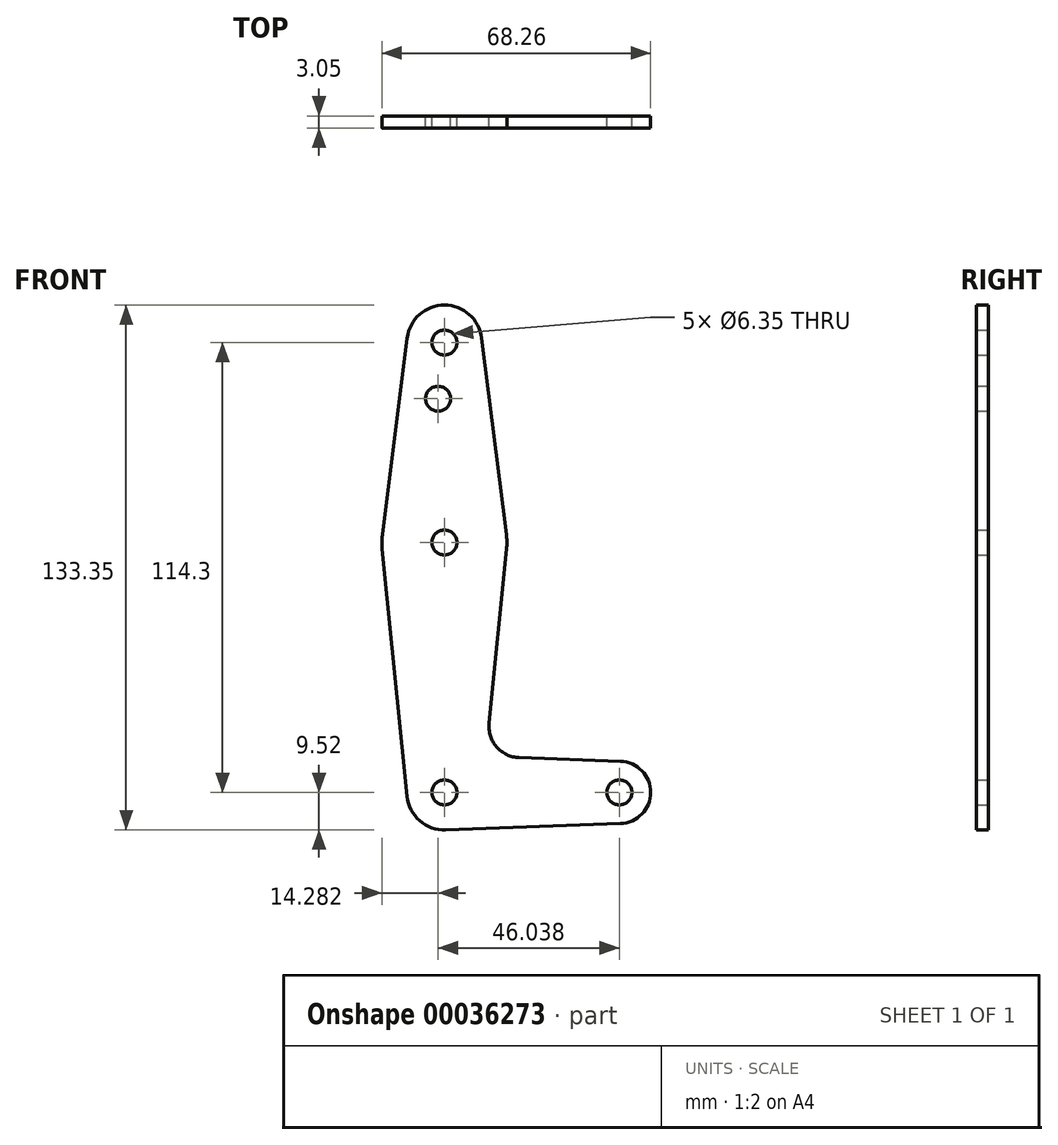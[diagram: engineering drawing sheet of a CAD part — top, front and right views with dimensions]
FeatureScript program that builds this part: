
annotation { "Feature Type Name" : "Feature", "Feature Type Description" : "" }
export const myFeature = defineFeature(function(context is Context, id is Id, definition is map)
    precondition{}
    {
        {
            var Q0;
            Q0=qCreatedBy(makeId("Front.planeOp"),FACE);
            var sketch = newSketch(context, id + "F0", { "sketchPlane" : qUnion([Q0])});
            skCircle(sketch, "E0", {"center": v(0, 0) * mm, "radius": 9.53 * mm});
            skCircle(sketch, "E1", {"center": v(0, 63.5) * mm, "radius": 15.88 * mm});
            skCircle(sketch, "E2", {"center": v(0, 114.3) * mm, "radius": 9.53 * mm});
            skCircle(sketch, "E3", {"center": v(44.45, 0) * mm, "radius": 7.94 * mm});
            skLineSegment(sketch, "E4", {"start": v(0, 114.3) * mm, "end": v(0, 0) * mm, "construction": true});
            skLineSegment(sketch, "E5", {"start": v(0, 0) * mm, "end": v(44.45, 0) * mm, "construction": true});
            skLineSegment(sketch, "E6", {"start": v(-9.45, 115.5) * mm, "end": v(-15.75, 65.48) * mm});
            skLineSegment(sketch, "E7", {"start": v(-15.8, 61.91) * mm, "end": v(-9.48, -0.95) * mm});
            skLineSegment(sketch, "E8", {"start": v(9.45, 115.5) * mm, "end": v(15.75, 65.48) * mm});
            skLineSegment(sketch, "E9", {"start": v(15.8, 61.91) * mm, "end": v(11.34, 17.6) * mm});
            skLineSegment(sketch, "E10", {"start": v(18.97, 8.85) * mm, "end": v(44.73, 7.93) * mm});
            skLineSegment(sketch, "E11", {"start": v(0.34, -9.52) * mm, "end": v(44.73, -7.93) * mm});
            skCircle(sketch, "E12", {"center": v(0, 114.3) * mm, "radius": 3.18 * mm});
            skCircle(sketch, "E13", {"center": v(0, 63.5) * mm, "radius": 3.18 * mm});
            skCircle(sketch, "E14", {"center": v(0, 0) * mm, "radius": 3.18 * mm});
            skCircle(sketch, "E15", {"center": v(44.45, 0) * mm, "radius": 3.18 * mm});
            skCircle(sketch, "E16", {"center": v(-1.59, 100.03) * mm, "radius": 3.18 * mm});
            skArc(sketch, "E17.filletArc", {"start": v(11.34, 17.6) * mm, "mid": v(13.26, 11.57) * mm, "end": v(18.97, 8.85) * mm});
            skSolve(sketch);
        }
        {
            var Q0;
            Q0 = qSketchRegion(id + "F0", true);
            extrude(context, id + "F1", {"entities" : qUnion([Q0]), "depth" : 3.05 * mm});
        }
    });
